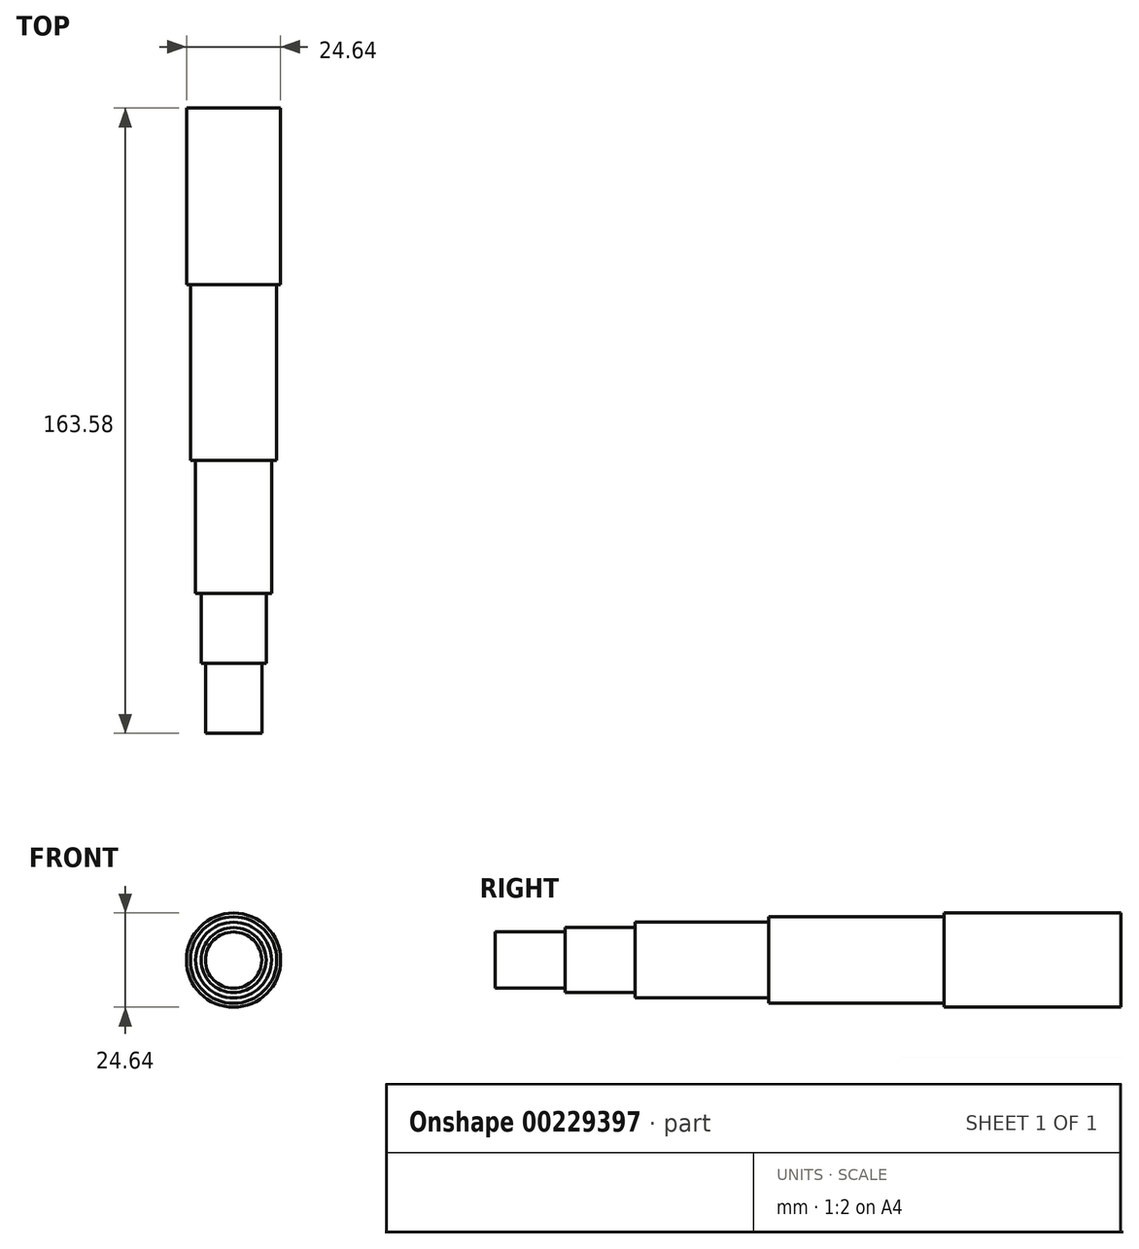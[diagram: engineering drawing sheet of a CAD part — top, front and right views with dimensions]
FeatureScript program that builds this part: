
annotation { "Feature Type Name" : "Feature", "Feature Type Description" : "" }
export const myFeature = defineFeature(function(context is Context, id is Id, definition is map)
    precondition{}
    {
        {
            var Q0;
            Q0=qCreatedBy(makeId("Front.planeOp"),FACE);
            var sketch = newSketch(context, id + "F0", { "sketchPlane" : qUnion([Q0])});
            skCircle(sketch, "E0", {"center": v(-7.64, 0) * mm, "radius": 12.74 * mm});
            skCircle(sketch, "E1", {"center": v(-7.64, 0) * mm, "radius": 12.32 * mm});
            skSolve(sketch);
        }
        {
            var Q0;
            Q0=makeQuery(id+"F0.imprint","IMPRINT",FACE,{"disambiguationData":[TD([[makeQuery(id+"F0.imprint","IMPRINT",EDGE,{"derivedFrom":sQuery(id+"F0.wireOp",EDGE,"E1")}),1.0]])]});
            extrude(context, id + "F1", {"entities" : qUnion([Q0]), "depth" : 46.22 * mm});
        }
        {
            var Q0;
            Q0=makeQuery(id+"F1.opExtrude","CAP_FACE",FACE,{"disambiguationData":[OSD([sQuery(id+"F0.wireOp",EDGE,"E1")])],"isStart":false});
            var sketch = newSketch(context, id + "F2", { "sketchPlane" : qUnion([Q0])});
            skCircle(sketch, "E2", {"center": v(-7.64, 0) * mm, "radius": 11.67 * mm});
            skCircle(sketch, "E3", {"center": v(-7.64, 0) * mm, "radius": 11.3 * mm});
            skSolve(sketch);
        }
        {
            var Q0;
            Q0=makeQuery(id+"F2.imprint","IMPRINT",FACE,{"disambiguationData":[TD([[makeQuery(id+"F2.imprint","IMPRINT",EDGE,{"derivedFrom":sQuery(id+"F2.wireOp",EDGE,"E3")}),1.0]])]});
            extrude(context, id + "F3", {"entities" : qUnion([Q0]), "operationType" : NewBodyOperationType.ADD, "depth" : 45.9 * mm});
        }
        {
            var Q0;
            Q0=makeQuery(id+"F3.opExtrude","CAP_FACE",FACE,{"disambiguationData":[OSD([sQuery(id+"F2.wireOp",EDGE,"E3")])],"isStart":false});
            var sketch = newSketch(context, id + "F4", { "sketchPlane" : qUnion([Q0])});
            skCircle(sketch, "E4", {"center": v(-7.64, 0) * mm, "radius": 9.9 * mm});
            skCircle(sketch, "E5", {"center": v(-7.64, 0) * mm, "radius": 10.35 * mm});
            skSolve(sketch);
        }
        {
            var Q0;
            Q0=makeQuery(id+"F4.imprint","IMPRINT",FACE,{"disambiguationData":[TD([[makeQuery(id+"F4.imprint","IMPRINT",EDGE,{"derivedFrom":sQuery(id+"F4.wireOp",EDGE,"E4")}),1.0]])]});
            extrude(context, id + "F5", {"entities" : qUnion([Q0]), "operationType" : NewBodyOperationType.ADD, "depth" : 34.88 * mm});
        }
        {
            var Q0;
            Q0=makeQuery(id+"F5.opExtrude","CAP_FACE",FACE,{"disambiguationData":[OSD([sQuery(id+"F4.wireOp",EDGE,"E4")])],"isStart":false});
            var sketch = newSketch(context, id + "F6", { "sketchPlane" : qUnion([Q0])});
            skCircle(sketch, "E6", {"center": v(-7.64, 0) * mm, "radius": 8.5 * mm});
            skCircle(sketch, "E7", {"center": v(-7.64, 0) * mm, "radius": 8.86 * mm});
            skSolve(sketch);
        }
        {
            var Q0;
            Q0=makeQuery(id+"F6.imprint","IMPRINT",FACE,{"disambiguationData":[TD([[makeQuery(id+"F6.imprint","IMPRINT",EDGE,{"derivedFrom":sQuery(id+"F6.wireOp",EDGE,"E6")}),1.0]])]});
            extrude(context, id + "F7", {"entities" : qUnion([Q0]), "operationType" : NewBodyOperationType.ADD, "depth" : 18.3 * mm});
        }
        {
            var Q0;
            Q0=makeQuery(id+"F7.opExtrude","CAP_FACE",FACE,{"disambiguationData":[OSD([sQuery(id+"F6.wireOp",EDGE,"E6")])],"isStart":false});
            var sketch = newSketch(context, id + "F8", { "sketchPlane" : qUnion([Q0])});
            skCircle(sketch, "E8", {"center": v(-7.64, 0) * mm, "radius": 7.37 * mm});
            skCircle(sketch, "E9", {"center": v(-7.64, 0) * mm, "radius": 7.64 * mm});
            skSolve(sketch);
        }
        {
            var Q0;
            Q0=makeQuery(id+"F8.imprint","IMPRINT",FACE,{"disambiguationData":[TD([[makeQuery(id+"F8.imprint","IMPRINT",EDGE,{"derivedFrom":sQuery(id+"F8.wireOp",EDGE,"E8")}),1.0]])]});
            extrude(context, id + "F9", {"entities" : qUnion([Q0]), "operationType" : NewBodyOperationType.ADD, "depth" : 18.28 * mm});
        }
    });
